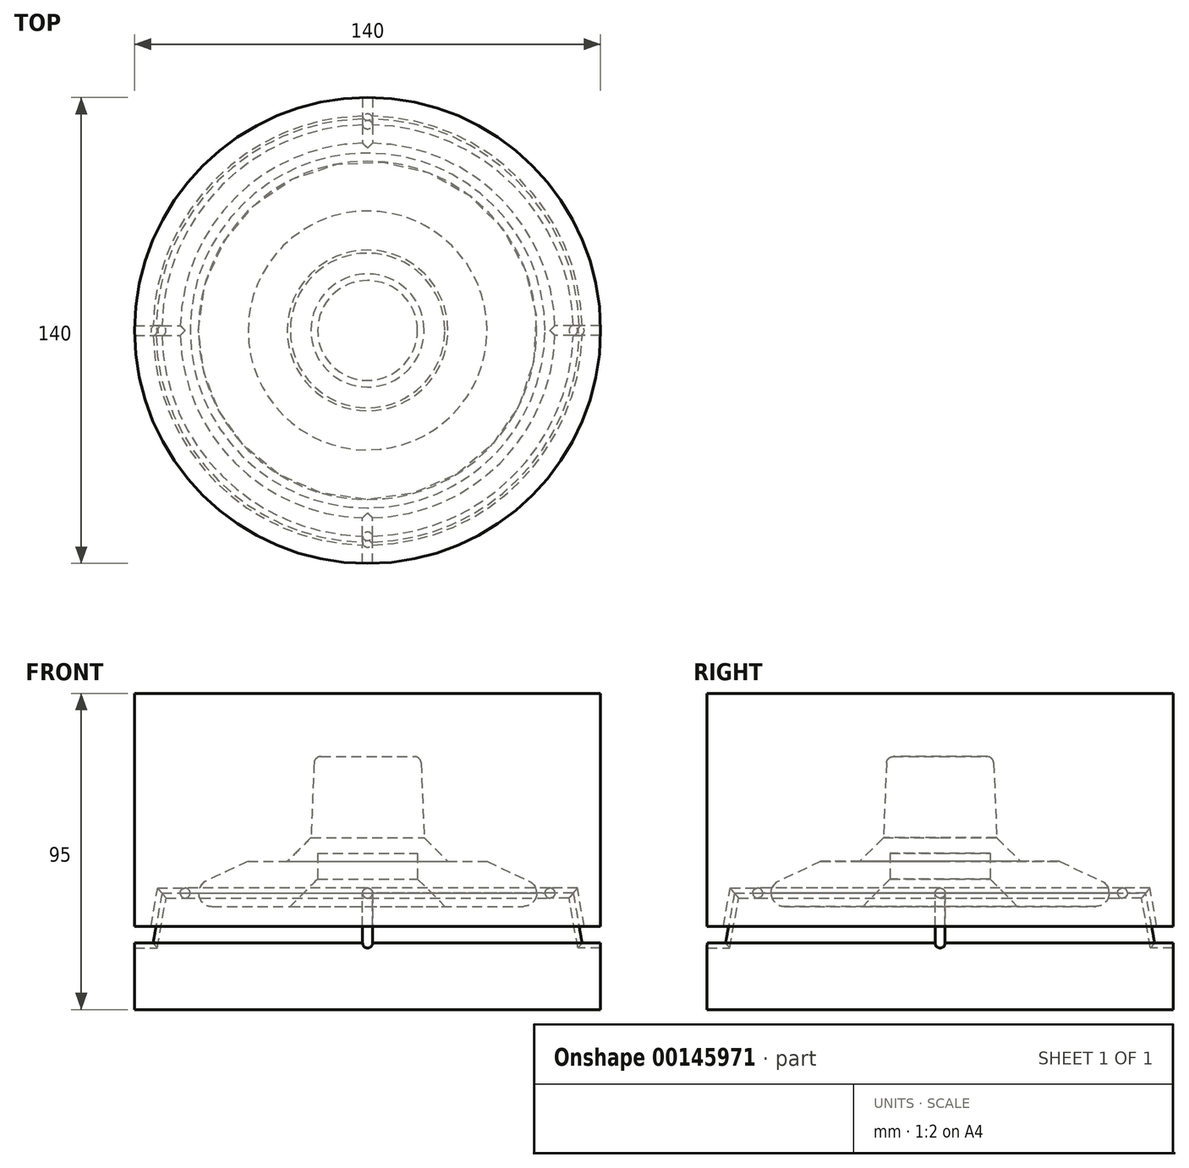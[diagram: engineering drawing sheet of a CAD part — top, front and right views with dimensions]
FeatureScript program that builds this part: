
annotation { "Feature Type Name" : "Feature", "Feature Type Description" : "" }
export const myFeature = defineFeature(function(context is Context, id is Id, definition is map)
    precondition{}
    {
        {
            var Q0;
            Q0=qCreatedBy(makeId("Front.planeOp"),FACE);
            var sketch = newSketch(context, id + "F0", { "sketchPlane" : qUnion([Q0])});
            skLineSegment(sketch, "E0", {"start": v(0, 52.85) * mm, "end": v(0, -46.13) * mm, "construction": true});
            skLineSegment(sketch, "E1", {"start": v(0, 37.3) * mm, "end": v(-16, 37.3) * mm});
            skLineSegment(sketch, "E2", {"start": v(-16, 37.3) * mm, "end": v(-17, 12.94) * mm});
            skLineSegment(sketch, "E3", {"start": v(-17, 12.94) * mm, "end": v(-24.15, 5.8) * mm});
            skLineSegment(sketch, "E4", {"start": v(-46.8, -7.7) * mm, "end": v(-23.23, -7.7) * mm});
            skLineSegment(sketch, "E5", {"start": v(0, -7.7) * mm, "end": v(0, 37.3) * mm});
            skLineSegment(sketch, "E6.MirrorCS", {"start": v(24.15, 5.8) * mm, "end": v(35.9, 5.8) * mm});
            skLineSegment(sketch, "E7.MirrorCS", {"start": v(16, 37.3) * mm, "end": v(17, 12.94) * mm});
            skLineSegment(sketch, "E8.MirrorCS", {"start": v(0, 37.3) * mm, "end": v(16, 37.3) * mm});
            skLineSegment(sketch, "E9.MirrorCS", {"start": v(45.33, -7.7) * mm, "end": v(15, -7.7) * mm});
            skLineSegment(sketch, "E10.MirrorCS", {"start": v(17, 12.94) * mm, "end": v(24.15, 5.8) * mm});
            skCircle(sketch, "E11", {"center": v(-46.8, -3.7) * mm, "radius": 4 * mm});
            skLineSegment(sketch, "E12", {"start": v(-35.9, 5.8) * mm, "end": v(-48.5, -0.08) * mm});
            skLineSegment(sketch, "E13.MirrorCS", {"start": v(35.9, 5.8) * mm, "end": v(48, 0.15) * mm});
            skCircle(sketch, "E14.MirrorC", {"center": v(46.8, -3.7) * mm, "radius": 4 * mm});
            skLineSegment(sketch, "E15", {"start": v(-35.9, 5.8) * mm, "end": v(-24.15, 5.8) * mm});
            skLineSegment(sketch, "E16", {"start": v(50.8, -3.55) * mm, "end": v(50.8, 7.86) * mm, "construction": true});
            skPoint(sketch, "E17.orphan", {"position": v(-48, 0.15) * mm});
            skLineSegment(sketch, "E18.bottom", {"start": v(15, 8.3) * mm, "end": v(-15, 8.3) * mm});
            skLineSegment(sketch, "E18.left", {"start": v(15, 8.3) * mm, "end": v(15, -8.3) * mm});
            skLineSegment(sketch, "E18.right", {"start": v(-15, 8.3) * mm, "end": v(-15, 0.53) * mm});
            skPoint(sketch, "E18.middle", {"position": v(0, 0) * mm});
            skPoint(sketch, "E19", {"position": v(15, -7.7) * mm});
            skPoint(sketch, "E20", {"position": v(0, 8.3) * mm});
            skLineSegment(sketch, "E21", {"start": v(-15, 0.53) * mm, "end": v(-23.23, -7.7) * mm});
            skLineSegment(sketch, "E22", {"start": v(0, -3.7) * mm, "end": v(0, 56.3) * mm});
            skLineSegment(sketch, "E23", {"start": v(0, 56.3) * mm, "end": v(-70, 56.3) * mm});
            skLineSegment(sketch, "E24", {"start": v(-70, 56.3) * mm, "end": v(-70, -38.7) * mm});
            skLineSegment(sketch, "E25", {"start": v(-70, -38.7) * mm, "end": v(0, -38.7) * mm});
            skLineSegment(sketch, "E26", {"start": v(0, -38.7) * mm, "end": v(0, -3.7) * mm});
            skLineSegment(sketch, "E27", {"start": v(0, -3.7) * mm, "end": v(-70, -3.7) * mm});
            skCircle(sketch, "E28", {"center": v(-54.8, -3.7) * mm, "radius": 1.5 * mm});
            skLineSegment(sketch, "E29", {"start": v(-70, -13.7) * mm, "end": v(-63.56, -13.7) * mm});
            skLineSegment(sketch, "E30", {"start": v(-70, -18.7) * mm, "end": v(-64.44, -18.7) * mm});
            skLineSegment(sketch, "E31", {"start": v(-64.44, -18.7) * mm, "end": v(-61.8, -3.7) * mm});
            skPoint(sketch, "E32.orphan", {"position": v(-45.33, -7.7) * mm});
            skLineSegment(sketch, "E33", {"start": v(-54.8, -3.7) * mm, "end": v(-61.8, -3.7) * mm});
            skSolve(sketch);
        }
        {
            var Q0;
            Q0=makeQuery(id+"F0.imprint","IMPRINT",FACE,{"disambiguationData":[TD([[makeQuery(id+"F0.imprint","IMPRINT",EDGE,{"derivedFrom":sQuery(id+"F0.wireOp",EDGE,"E1")}),1.0]])]});
            var Q1;
            {var subQ0=sQuery(id+"F0.wireOp",EDGE,"E11");var subQ1=makeQuery(id+"F0.imprint","INTERSECT",VERTEX,{"derivedFrom":[sQuery(id+"F0.wireOp",EDGE,"E4"),subQ0]});Q1=makeQuery(id+"F0.imprint","IMPRINT",FACE,{"disambiguationData":[TD([[makeQuery(id+"F0.imprint","IMPRINT",EDGE,{"disambiguationData":[TD([[subQ1,1.0]])],"derivedFrom":subQ0}),1.0]])]});}
            var Q2;
            {var subQ0=sQuery(id+"F0.wireOp",EDGE,"E11");var subQ1=makeQuery(id+"F0.imprint","INTERSECT",VERTEX,{"derivedFrom":[subQ0,sQuery(id+"F0.wireOp",EDGE,"E12")]});Q2=makeQuery(id+"F0.imprint","IMPRINT",FACE,{"disambiguationData":[TD([[makeQuery(id+"F0.imprint","IMPRINT",EDGE,{"disambiguationData":[TD([[subQ1,1.0]])],"derivedFrom":subQ0}),1.0]])]});}
            var Q3;
            {var subQ0=sQuery(id+"F0.wireOp",EDGE,"E4");Q3=makeQuery(id+"F0.imprint","IMPRINT",FACE,{"disambiguationData":[TD([[makeQuery(id+"F0.imprint","IMPRINT",EDGE,{"derivedFrom":subQ0}),1.0]])]});}
            var Q4;
            Q4=sQuery(id+"F0.wireOp",EDGE,"E5");
            revolve(context, id + "F1", {"entities" : qUnion([Q0, Q1, Q2, Q3]), "axis" : qUnion([Q4]), "revolveType" : RevolveType.FULL});
        }
        {
            var Q0;
            Q0=makeQuery(id+"F1.opRevolve","SWEPT_EDGE",EDGE,{"disambiguationData":[OSD([sQuery(id+"F0.wireOp",EDGE,"E1"),sQuery(id+"F0.wireOp",EDGE,"E2")])]});
            fillet(context, id + "F2", {"entities" : qUnion([Q0]), "radius" : 2 * mm, "tangentPropagation" : true, "allowEdgeOverflow" : false});
        }
        {
            var Q0;
            {var subQ5=sQuery(id+"F0.wireOp",EDGE,"E1");Q0=makeQuery(id+"F0.imprint","IMPRINT",FACE,{"disambiguationData":[TD([[makeQuery(id+"F0.imprint","IMPRINT",EDGE,{"derivedFrom":subQ5}),-1.0]])]});}
            var Q1;
            {var subQ3=sQuery(id+"F0.wireOp",EDGE,"E29");Q1=makeQuery(id+"F0.imprint","IMPRINT",FACE,{"disambiguationData":[TD([[makeQuery(id+"F0.imprint","IMPRINT",EDGE,{"derivedFrom":subQ3}),1.0]])]});}
            var Q2;
            {var subQ0=sQuery(id+"F0.wireOp",EDGE,"E28");var subQ1=sQuery(id+"F0.wireOp",EDGE,"E27");var subQ2=makeQuery(id+"F0.imprint","INTERSECT",VERTEX,{"disambiguationData":[OD(0.0)],"derivedFrom":[subQ1,subQ0]});Q2=makeQuery(id+"F0.imprint","IMPRINT",FACE,{"disambiguationData":[TD([[makeQuery(id+"F0.imprint","IMPRINT",EDGE,{"disambiguationData":[TD([[subQ2,-1.0]])],"derivedFrom":subQ1}),-1.0]])]});}
            var Q3;
            Q3=sQuery(id+"F0.wireOp",EDGE,"E22");
            revolve(context, id + "F3", {"entities" : qUnion([Q0, Q1, Q2]), "axis" : qUnion([Q3]), "revolveType" : RevolveType.FULL});
        }
        {
            var Q0;
            {var subQ10=sQuery(id+"F0.wireOp",EDGE,"E4");Q0=makeQuery(id+"F0.imprint","IMPRINT",FACE,{"disambiguationData":[TD([[makeQuery(id+"F0.imprint","IMPRINT",EDGE,{"derivedFrom":subQ10}),-1.0]])]});}
            var Q1;
            {var subQ6=sQuery(id+"F0.wireOp",EDGE,"E18.right");Q1=makeQuery(id+"F0.imprint","IMPRINT",FACE,{"disambiguationData":[TD([[makeQuery(id+"F0.imprint","IMPRINT",EDGE,{"derivedFrom":subQ6}),1.0]])]});}
            var Q2;
            Q2=sQuery(id+"F0.wireOp",EDGE,"E5");
            revolve(context, id + "F4", {"entities" : qUnion([Q0, Q1]), "axis" : qUnion([Q2]), "revolveType" : RevolveType.FULL});
        }
        {
            var Q0;
            Q0=qCreatedBy(makeId("Right.planeOp"),FACE);
            cPlane(context, id + "F5", {"entities" : qUnion([Q0]), "cplaneType" : CPlaneType.OFFSET, "offset" : 70 * mm, "oppositeDirection" : true, "width" : 150 * mm, "height" : 150 * mm});
        }
        {
            var Q0;
            Q0=qCreatedBy(id+"F5.planeOp",FACE);
            var sketch = newSketch(context, id + "F6", { "sketchPlane" : qUnion([Q0])});
            skPoint(sketch, "E34.0", {"position": v(0, -18.7) * mm});
            skCircle(sketch, "E35", {"center": v(0, -18.7) * mm, "radius": 1.5 * mm});
            skSolve(sketch);
        }
        {
            var Q0;
            Q0=makeQuery(id+"F6.imprint","IMPRINT",FACE,{"disambiguationData":[TD([[makeQuery(id+"F6.imprint","IMPRINT",EDGE,{"derivedFrom":sQuery(id+"F6.wireOp",EDGE,"E35")}),1.0]])]});
            var Q1;
            Q1=sQuery(id+"F0.wireOp",EDGE,"E30");
            var Q2;
            Q2=sQuery(id+"F0.wireOp",EDGE,"E31");
            var Q3;
            Q3=sQuery(id+"F0.wireOp",EDGE,"E33");
            sweep(context, id + "F7", {"profiles" : qUnion([Q0]), "path" : qUnion([Q1, Q2, Q3])});
        }
        {
            var Q0;
            Q0=makeQuery(id+"F7.opSweep","SWEPT_BODY",BODY,{"disambiguationData":[OSD([sQuery(id+"F0.wireOp",EDGE,"E33"),sQuery(id+"F6.wireOp",EDGE,"E35")])]});
            var Q1;
            Q1=sQuery(id+"F0.wireOp",EDGE,"E22");
            circularPattern(context, id + "F8", {"operationType" : NewBodyOperationType.REMOVE, "entities" : qUnion([Q0]), "axis" : qUnion([Q1]), "angle" : 90 * degree, "instanceCount" : 4});
        }
        {
            var Q0;
            Q0=makeQuery(id+"F3.opRevolve","SWEPT_EDGE",EDGE,{"disambiguationData":[OSD([sQuery(id+"F0.wireOp",EDGE,"E1"),sQuery(id+"F0.wireOp",EDGE,"E2")])]});
            fillet(context, id + "F9", {"entities" : qUnion([Q0]), "radius" : 2 * mm, "tangentPropagation" : true, "allowEdgeOverflow" : false});
        }
    });
